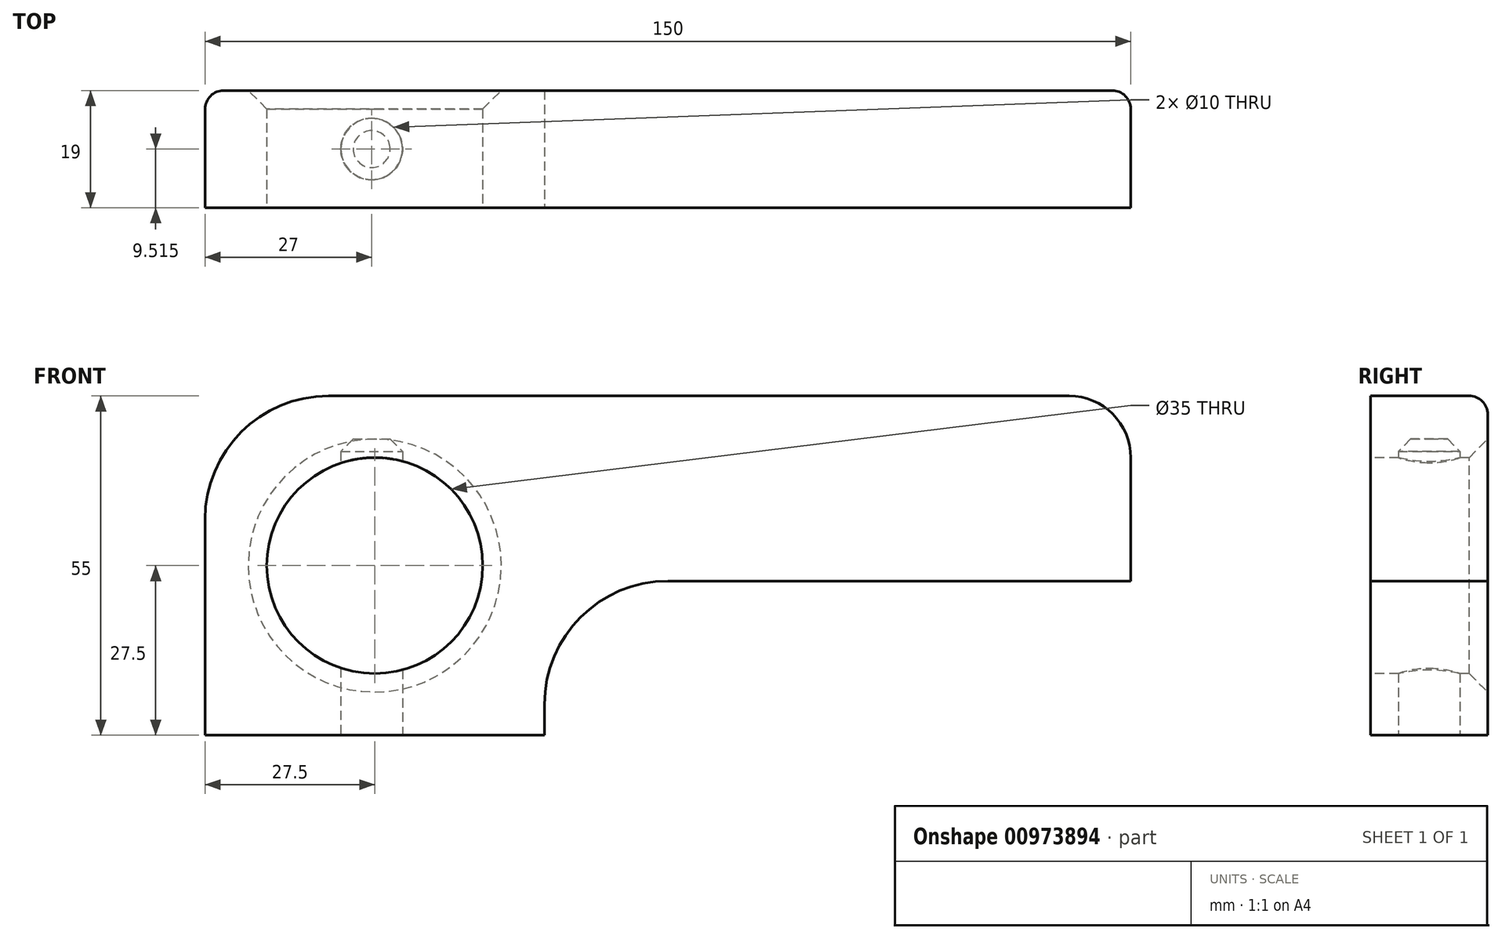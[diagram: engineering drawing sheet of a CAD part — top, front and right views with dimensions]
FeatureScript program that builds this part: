
annotation { "Feature Type Name" : "Feature", "Feature Type Description" : "" }
export const myFeature = defineFeature(function(context is Context, id is Id, definition is map)
    precondition{}
    {
        {
            var Q0;
            Q0=qCreatedBy(makeId("Front.planeOp"),FACE);
            var sketch = newSketch(context, id + "F0", { "sketchPlane" : qUnion([Q0])});
            skLineSegment(sketch, "E0.bottom", {"start": v(0, 0) * mm, "end": v(150, 0) * mm});
            skLineSegment(sketch, "E0.top", {"start": v(0, 55) * mm, "end": v(150, 55) * mm});
            skLineSegment(sketch, "E0.left", {"start": v(0, 0) * mm, "end": v(0, 55) * mm});
            skLineSegment(sketch, "E0.right", {"start": v(150, 0) * mm, "end": v(150, 55) * mm});
            skSolve(sketch);
        }
        {
            var Q0;
            Q0=makeQuery(id+"F0.imprint","IMPRINT",FACE,{"disambiguationData":[TD([[makeQuery(id+"F0.imprint","IMPRINT",EDGE,{"derivedFrom":sQuery(id+"F0.wireOp",EDGE,"E0.bottom")}),1.0]])]});
            extrude(context, id + "F1", {"entities" : qUnion([Q0]), "depth" : 19 * mm, "offsetDistance" : 25 * mm});
        }
        {
            var Q0;
            Q0=makeQuery(id+"F1.opExtrude","CAP_FACE",FACE,{"disambiguationData":[OSD([sQuery(id+"F0.wireOp",EDGE,"E0.bottom"),sQuery(id+"F0.wireOp",EDGE,"E0.top"),sQuery(id+"F0.wireOp",EDGE,"E0.left"),sQuery(id+"F0.wireOp",EDGE,"E0.right")])],"isStart":false});
            var sketch = newSketch(context, id + "F2", { "sketchPlane" : qUnion([Q0])});
            skCircle(sketch, "E1", {"center": v(27.5, 27.5) * mm, "radius": 17.5 * mm});
            skSolve(sketch);
        }
        {
            var Q0;
            Q0=makeQuery(id+"F2.imprint","IMPRINT",FACE,{"disambiguationData":[TD([[makeQuery(id+"F2.imprint","IMPRINT",EDGE,{"derivedFrom":sQuery(id+"F2.wireOp",EDGE,"E1")}),1.0]])]});
            extrude(context, id + "F3", {"entities" : qUnion([Q0]), "operationType" : NewBodyOperationType.REMOVE, "endBound" : BoundingType.THROUGH_ALL, "oppositeDirection" : true, "depth" : 25 * mm, "offsetDistance" : 25 * mm});
        }
        {
            var Q0;
            Q0=makeQuery(id+"F1.opExtrude","CAP_FACE",FACE,{"disambiguationData":[OSD([sQuery(id+"F0.wireOp",EDGE,"E0.bottom"),sQuery(id+"F0.wireOp",EDGE,"E0.top"),sQuery(id+"F0.wireOp",EDGE,"E0.left"),sQuery(id+"F0.wireOp",EDGE,"E0.right")])],"isStart":false});
            var sketch = newSketch(context, id + "F4", { "sketchPlane" : qUnion([Q0])});
            skLineSegment(sketch, "E2", {"start": v(55, 0) * mm, "end": v(55, 25) * mm});
            skLineSegment(sketch, "E3", {"start": v(55, 25) * mm, "end": v(150, 25) * mm});
            skSolve(sketch);
        }
        {
            var Q0;
            {var subQ0=sQuery(id+"F4.wireOp",EDGE,"E2");Q0=makeQuery(id+"F4.imprint","IMPRINT",FACE,{"disambiguationData":[TD([[makeQuery(id+"F4.imprint","IMPRINT",EDGE,{"derivedFrom":subQ0}),-1.0]])]});}
            extrude(context, id + "F5", {"entities" : qUnion([Q0]), "operationType" : NewBodyOperationType.REMOVE, "endBound" : BoundingType.THROUGH_ALL, "oppositeDirection" : true, "depth" : 25 * mm, "offsetDistance" : 25 * mm});
        }
        {
            var Q0;
            Q0=makeQuery(id+"F5.boolean.opBoolean","COPY",EDGE,{"derivedFrom":makeQuery(id+"F5.opExtrude","SWEPT_EDGE",EDGE,{"disambiguationData":[OSD([sQuery(id+"F4.wireOp",EDGE,"E2"),sQuery(id+"F4.wireOp",EDGE,"E3")])]})});
            var Q1;
            Q1=makeQuery(id+"F1.opExtrude","SWEPT_EDGE",EDGE,{"disambiguationData":[OSD([sQuery(id+"F0.wireOp",EDGE,"E0.top"),sQuery(id+"F0.wireOp",EDGE,"E0.left")])]});
            fillet(context, id + "F6", {"entities" : qUnion([Q0, Q1]), "radius" : 20 * mm, "tangentPropagation" : true, "allowEdgeOverflow" : false});
        }
        {
            var Q0;
            Q0=makeQuery(id+"F5.boolean.opBoolean","COPY",EDGE,{"derivedFrom":makeQuery(id+"F5.opExtrude","SWEPT_EDGE",EDGE,{"disambiguationData":[OSD([sQuery(id+"F0.wireOp",EDGE,"E0.right"),sQuery(id+"F4.wireOp",EDGE,"E3")])]})});
            var Q1;
            Q1=makeQuery(id+"F1.opExtrude","SWEPT_EDGE",EDGE,{"disambiguationData":[OSD([sQuery(id+"F0.wireOp",EDGE,"E0.top"),sQuery(id+"F0.wireOp",EDGE,"E0.right")])]});
            fillet(context, id + "F7", {"entities" : qUnion([Q0, Q1]), "radius" : 10 * mm, "tangentPropagation" : true, "allowEdgeOverflow" : false});
        }
        {
            var Q0;
            Q0=makeQuery(id+"F5.boolean.opBoolean","COPY",EDGE,{"derivedFrom":makeQuery(id+"F5.opExtrude","CAP_EDGE",EDGE,{"disambiguationData":[OSD([sQuery(id+"F4.wireOp",EDGE,"E3")])],"isStart":true})});
            var Q1;
            Q1=makeQuery(id+"F1.opExtrude","CAP_EDGE",EDGE,{"disambiguationData":[OSD([sQuery(id+"F0.wireOp",EDGE,"E0.top")])],"isStart":true});
            fillet(context, id + "F8", {"entities" : qUnion([Q0, Q1]), "radius" : 3 * mm, "tangentPropagation" : true, "allowEdgeOverflow" : false});
        }
        {
            var Q0;
            Q0=makeQuery(id+"F1.opExtrude","SWEPT_FACE",FACE,{"disambiguationData":[OSD([sQuery(id+"F0.wireOp",EDGE,"E0.bottom")])]});
            var sketch = newSketch(context, id + "F9", { "sketchPlane" : qUnion([Q0])});
            skCircle(sketch, "E4", {"center": v(27, 9.48) * mm, "radius": 5 * mm});
            skSolve(sketch);
        }
        {
            var Q0;
            Q0=makeQuery(id+"F9.imprint","IMPRINT",FACE,{"disambiguationData":[TD([[makeQuery(id+"F9.imprint","IMPRINT",EDGE,{"derivedFrom":sQuery(id+"F9.wireOp",EDGE,"E4")}),1.0]])]});
            extrude(context, id + "F10", {"entities" : qUnion([Q0]), "operationType" : NewBodyOperationType.REMOVE, "oppositeDirection" : true, "depth" : 48 * mm, "offsetDistance" : 25 * mm});
        }
        {
            var Q0;
            Q0=makeQuery(id+"F3.boolean.opBoolean","COPY",EDGE,{"derivedFrom":makeQuery(id+"F3.opExtrude","CAP_EDGE",EDGE,{"disambiguationData":[OSD([sQuery(id+"F2.wireOp",EDGE,"E1")])],"isStart":true})});
            var Q1;
            Q1=makeQuery(id+"F3.boolean.opBoolean","INTERSECT",EDGE,{"derivedFrom":[makeQuery(id+"F1.opExtrude","CAP_FACE",FACE,{"disambiguationData":[OSD([sQuery(id+"F0.wireOp",EDGE,"E0.bottom"),sQuery(id+"F0.wireOp",EDGE,"E0.top"),sQuery(id+"F0.wireOp",EDGE,"E0.left"),sQuery(id+"F0.wireOp",EDGE,"E0.right")])],"isStart":true}),makeQuery(id+"F3.opExtrude","SWEPT_FACE",FACE,{"disambiguationData":[OSD([sQuery(id+"F2.wireOp",EDGE,"E1")])]})]});
            chamfer(context, id + "F11", {"entities" : qUnion([Q0, Q1]), "width" : 3 * mm, "tangentPropagation" : true});
        }
        {
            var Q0;
            Q0=makeQuery(id+"F10.boolean.opBoolean","COPY",EDGE,{"derivedFrom":makeQuery(id+"F10.opExtrude","CAP_EDGE",EDGE,{"disambiguationData":[OSD([sQuery(id+"F9.wireOp",EDGE,"E4")])],"isStart":false})});
            chamfer(context, id + "F12", {"entities" : qUnion([Q0]), "width" : 2 * mm, "tangentPropagation" : true});
        }
    });
